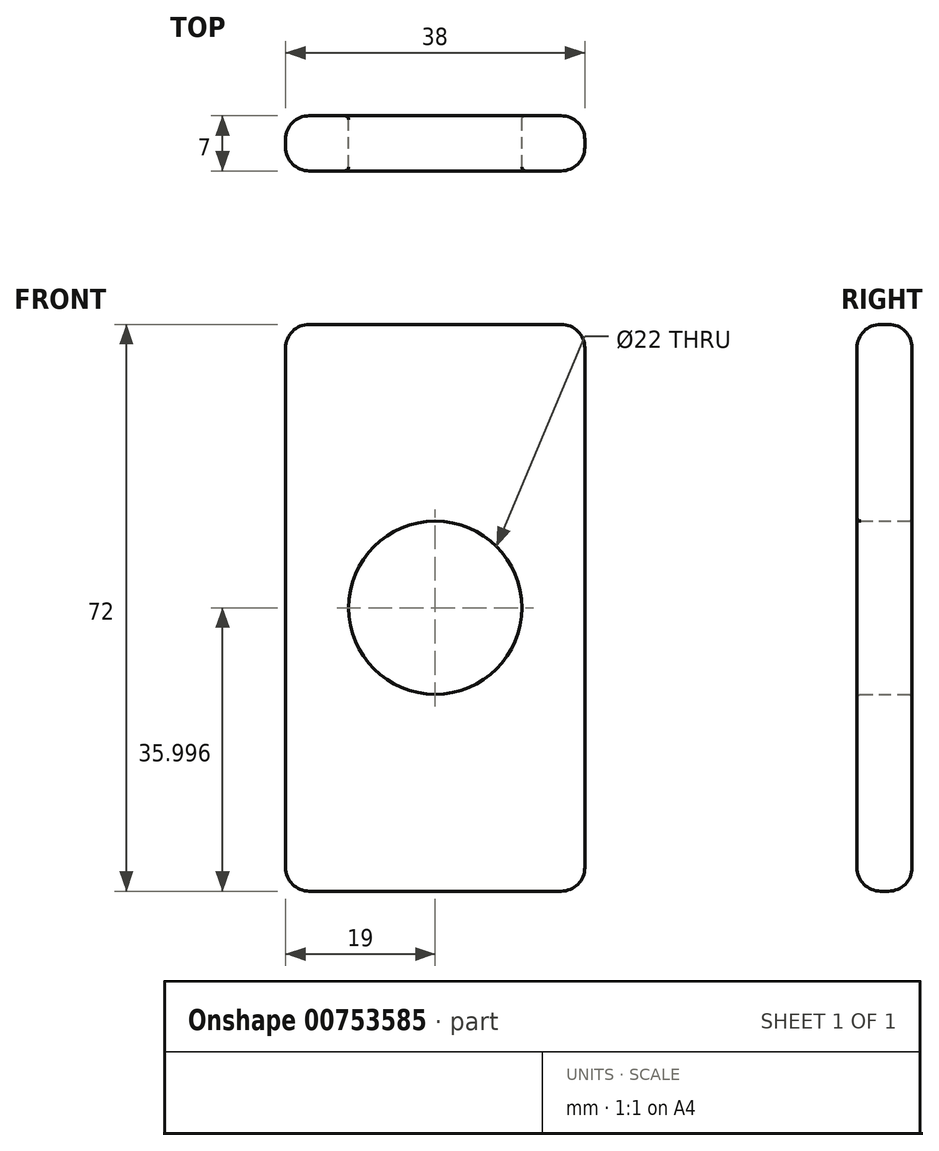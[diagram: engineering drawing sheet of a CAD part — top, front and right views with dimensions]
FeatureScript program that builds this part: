
annotation { "Feature Type Name" : "Feature", "Feature Type Description" : "" }
export const myFeature = defineFeature(function(context is Context, id is Id, definition is map)
    precondition{}
    {
        {
            var Q0;
            Q0=qCreatedBy(makeId("Front.planeOp"),FACE);
            var sketch = newSketch(context, id + "F0", { "sketchPlane" : qUnion([Q0])});
            skLineSegment(sketch, "E0", {"start": v(0, 55.32) * mm, "end": v(-19, 55.32) * mm});
            skLineSegment(sketch, "E1", {"start": v(-19, 55.32) * mm, "end": v(-19, -16.68) * mm});
            skLineSegment(sketch, "E2", {"start": v(-19, -16.68) * mm, "end": v(0, -16.68) * mm});
            skLineSegment(sketch, "E3.MirrorCS", {"start": v(19, 55.32) * mm, "end": v(19, -16.68) * mm});
            skLineSegment(sketch, "E4.MirrorCS", {"start": v(0, 55.32) * mm, "end": v(19, 55.32) * mm});
            skLineSegment(sketch, "E5.MirrorCS", {"start": v(19, -16.68) * mm, "end": v(0, -16.68) * mm});
            skLineSegment(sketch, "E6", {"start": v(0, 55.32) * mm, "end": v(0, -16.68) * mm, "construction": true});
            skCircle(sketch, "E7", {"center": v(0, 19.32) * mm, "radius": 11 * mm});
            skSolve(sketch);
        }
        {
            var Q0;
            Q0=makeQuery(id+"F0.imprint","IMPRINT",FACE,{"disambiguationData":[TD([[makeQuery(id+"F0.imprint","IMPRINT",EDGE,{"derivedFrom":sQuery(id+"F0.wireOp",EDGE,"E0")}),1.0]])]});
            extrude(context, id + "F1", {"entities" : qUnion([Q0]), "depth" : 7 * mm, "offsetDistance" : 25.4 * mm});
        }
        {
            var Q0;
            Q0=makeQuery(id+"F1.opExtrude","CAP_EDGE",EDGE,{"disambiguationData":[OSD([sQuery(id+"F0.wireOp",EDGE,"E0"),sQuery(id+"F0.wireOp",EDGE,"E4.MirrorCS")])],"isStart":false});
            var Q1;
            Q1=makeQuery(id+"F1.opExtrude","CAP_EDGE",EDGE,{"disambiguationData":[OSD([sQuery(id+"F0.wireOp",EDGE,"E0"),sQuery(id+"F0.wireOp",EDGE,"E4.MirrorCS")])],"isStart":true});
            var Q2;
            Q2=makeQuery(id+"F1.opExtrude","CAP_EDGE",EDGE,{"disambiguationData":[OSD([sQuery(id+"F0.wireOp",EDGE,"E3.MirrorCS")])],"isStart":true});
            var Q3;
            Q3=makeQuery(id+"F1.opExtrude","CAP_EDGE",EDGE,{"disambiguationData":[OSD([sQuery(id+"F0.wireOp",EDGE,"E1")])],"isStart":false});
            var Q4;
            Q4=makeQuery(id+"F1.opExtrude","CAP_EDGE",EDGE,{"disambiguationData":[OSD([sQuery(id+"F0.wireOp",EDGE,"E3.MirrorCS")])],"isStart":false});
            var Q5;
            Q5=makeQuery(id+"F1.opExtrude","CAP_EDGE",EDGE,{"disambiguationData":[OSD([sQuery(id+"F0.wireOp",EDGE,"E2"),sQuery(id+"F0.wireOp",EDGE,"E5.MirrorCS")])],"isStart":false});
            var Q6;
            Q6=makeQuery(id+"F1.opExtrude","CAP_EDGE",EDGE,{"disambiguationData":[OSD([sQuery(id+"F0.wireOp",EDGE,"E2"),sQuery(id+"F0.wireOp",EDGE,"E5.MirrorCS")])],"isStart":true});
            var Q7;
            Q7=makeQuery(id+"F1.opExtrude","SWEPT_EDGE",EDGE,{"disambiguationData":[OSD([sQuery(id+"F0.wireOp",EDGE,"E3.MirrorCS"),sQuery(id+"F0.wireOp",EDGE,"E5.MirrorCS")])]});
            var Q8;
            Q8=makeQuery(id+"F1.opExtrude","SWEPT_EDGE",EDGE,{"disambiguationData":[OSD([sQuery(id+"F0.wireOp",EDGE,"E1"),sQuery(id+"F0.wireOp",EDGE,"E2")])]});
            var Q9;
            Q9=makeQuery(id+"F1.opExtrude","CAP_EDGE",EDGE,{"disambiguationData":[OSD([sQuery(id+"F0.wireOp",EDGE,"E1")])],"isStart":true});
            var Q10;
            Q10=makeQuery(id+"F1.opExtrude","SWEPT_EDGE",EDGE,{"disambiguationData":[OSD([sQuery(id+"F0.wireOp",EDGE,"E0"),sQuery(id+"F0.wireOp",EDGE,"E1")])]});
            var Q11;
            Q11=makeQuery(id+"F1.opExtrude","SWEPT_EDGE",EDGE,{"disambiguationData":[OSD([sQuery(id+"F0.wireOp",EDGE,"E3.MirrorCS"),sQuery(id+"F0.wireOp",EDGE,"E4.MirrorCS")])]});
            fillet(context, id + "F2", {"entities" : qUnion([Q0, Q1, Q2, Q3, Q4, Q5, Q6, Q7, Q8, Q9, Q10, Q11]), "radius" : 3 * mm, "tangentPropagation" : true, "allowEdgeOverflow" : false});
        }
        {
            var Q0;
            Q0=makeQuery(id+"F1.opExtrude","CAP_EDGE",EDGE,{"disambiguationData":[OSD([sQuery(id+"F0.wireOp",EDGE,"E7")])],"isStart":false});
            var Q1;
            Q1=makeQuery(id+"F1.opExtrude","CAP_EDGE",EDGE,{"disambiguationData":[OSD([sQuery(id+"F0.wireOp",EDGE,"E7")])],"isStart":true});
            fillet(context, id + "F3", {"entities" : qUnion([Q0, Q1]), "radius" : .5 * mm, "tangentPropagation" : true, "allowEdgeOverflow" : false});
        }
    });
